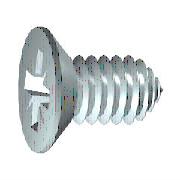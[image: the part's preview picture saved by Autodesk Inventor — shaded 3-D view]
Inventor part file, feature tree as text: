
AUTODESK INVENTOR PART (.ipt)
format: ipt  version: 2020 (Build 240168000, 168)  size: 268,288 bytes
history: native  units: mm (DEFAULTED — no unit token found)
features: extrude x2, plane x1, sketch x1
ambient origin geometry x8: Origin, YZ Plane, XZ Plane, XY Plane, X Axis, Y Axis, Z Axis, Center Point
bodies: Solid1 (feature_tree), Body (feature_tree)
feature tree (4):
  extrude  "Slot"  TaperAngle=45.0deg  [1 undecoded]
  extrude  "Star Cut"  Depth=2.05mm
  plane  "Work Plane2"
  sketch  "Sketch3"  dims[d0=16.0mm d2=45.0deg d3=3.5mm d5=7.3mm d6=4.1mm d7=4.625123mm d8=10.821041mm d9=2.2mm d16=90.0deg d10=45.0deg d11=1.64mm d12=4.1mm d13=0.515mm d14=4.1mm d15=45.0deg d17=0.515mm d18=2.35mm d19=-5.235988mm d20=13.65mm d21=0.0mm d22=1.75mm d23=3.2mm d25=0.0mm d26=2.05mm d66=25.4mm d27=0.872665mm d28=0.206mm d29=2.35mm d71=45.0deg d73=0.0mm d74=0.0mm]
note: 1 required parameter value undecoded (feature->parameter linkage not recoverable at this tier; creation-order binding heuristic only, values carry confidence <= 0.55)
